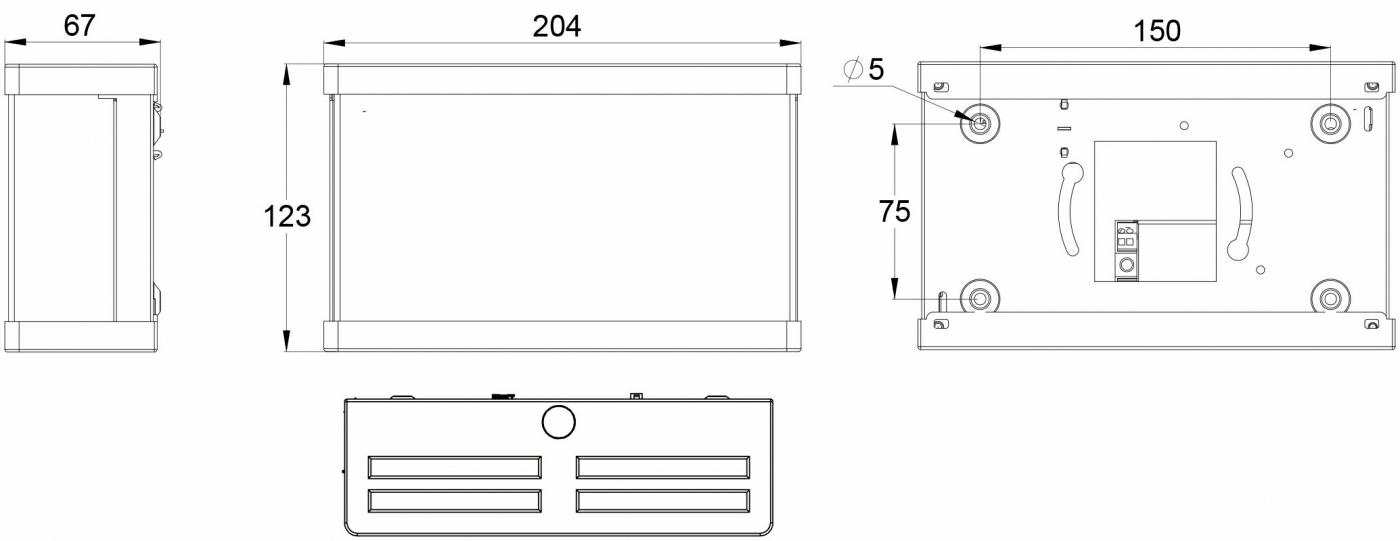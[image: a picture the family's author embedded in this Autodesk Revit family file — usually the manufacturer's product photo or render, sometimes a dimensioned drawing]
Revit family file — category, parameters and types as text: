
# Revit family: ESC 0,5 LED EMERGENCY EXIT LIGHT TW41651WK
name_source: partatom
category: Electrical Fixtures
revit_build: Autodesk Revit 2015 (Build: 20160512_0715(x64)
units: mm (PartAtom-declared; Revit-internal decimal feet)

## types (3) — shared parameters
Depth = 67 mm  [stored 0.219816 ft]
Height = 123 mm  [stored 0.403543 ft]
Manufacturer = Teknoware Oy
Model = ESC 0.5
Product Code = TW41651WK
Viewing Distance = 20000 mm  [stored 65.6168 ft]
Width = 204 mm

## per-type parameters (varying)
| type | Down | Left | Pictogram | Right | Type Comments |
| -arrow left | No | Yes | Teknoware Pictogram PB4161BE | No | PB4161BE |
| -arrow right | No | No | Teknoware Pictogram PB4162BE | Yes | PB4162BE |
| -arrow down | Yes | No | Teknoware Pictogram PB4171BE | No | PB4171BE |

note: [stored X ft] marks values corroborated as IEEE doubles in the binary element streams (Revit-internal decimal feet)

## geometry (parser evidence)
native form markers: Blend x6, Sweep x10
no freeform markers — native parametric forms only
